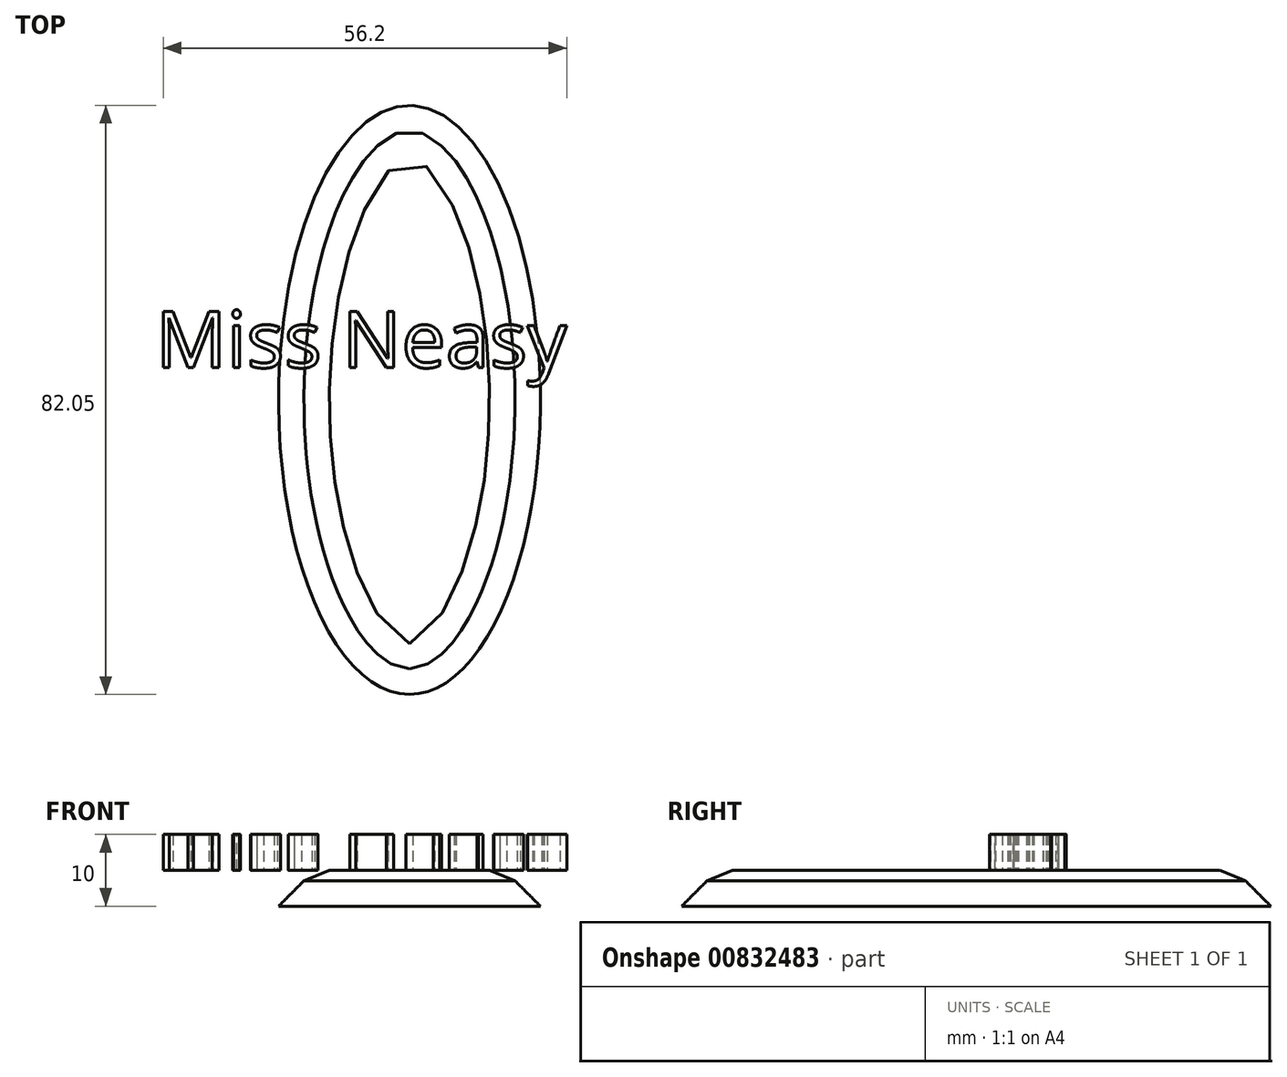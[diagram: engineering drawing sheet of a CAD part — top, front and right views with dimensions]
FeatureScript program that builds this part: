
annotation { "Feature Type Name" : "Feature", "Feature Type Description" : "" }
export const myFeature = defineFeature(function(context is Context, id is Id, definition is map)
    precondition{}
    {
        {
            var Q0;
            Q0=qCreatedBy(makeId("Top.planeOp"),FACE);
            var sketch = newSketch(context, id + "F0", { "sketchPlane" : qUnion([Q0])});
            skEllipse(sketch, "E0", {"center": v(-12.25, 46.89) * mm, "majorRadius": 41.03 * mm, "minorRadius": 18.23 * mm, "majorAxis": v(0, -1)});
            skSolve(sketch);
        }
        {
            var Q0;
            Q0=makeQuery(id+"F0.imprint","IMPRINT",FACE,{"disambiguationData":[TD([[makeQuery(id+"F0.imprint","IMPRINT",EDGE,{"derivedFrom":sQuery(id+"F0.wireOp",EDGE,"E0")}),1.0]])]});
            var sketch = newSketch(context, id + "F1", { "sketchPlane" : qUnion([Q0])});
            skLineSegment(sketch, "E1", {"start": v(-29.07, 38.27) * mm, "end": v(-13.53, -50.59) * mm});
            skLineSegment(sketch, "E2", {"start": v(-13.53, -50.59) * mm, "end": v(6.03, 41.56) * mm});
            skLineSegment(sketch, "E3", {"start": v(6.03, 41.56) * mm, "end": v(-29.07, 38.27) * mm});
            skSolve(sketch);
        }
        {
            var Q0;
            {var subQ0=sQuery(id+"F1.wireOp",EDGE,"E2");var subQ1=sQuery(id+"F1.wireOp",EDGE,"E1");var subQ2=makeQuery(id+"F1.imprint","INTERSECT",VERTEX,{"derivedFrom":[subQ1,subQ0]});Q0=makeQuery(id+"F1.imprint","IMPRINT",FACE,{"disambiguationData":[TD([[makeQuery(id+"F1.imprint","IMPRINT",EDGE,{"disambiguationData":[TD([[subQ2,1.0]])],"derivedFrom":subQ1}),1.0]])]});}
            var sketch = newSketch(context, id + "F2", { "sketchPlane" : qUnion([Q0])});
            skSolve(sketch);
        }
        {
            var Q0;
            {var subQ0=sQuery(id+"F1.wireOp",EDGE,"E2");var subQ1=sQuery(id+"F1.wireOp",EDGE,"E1");var subQ2=makeQuery(id+"F1.imprint","INTERSECT",VERTEX,{"derivedFrom":[subQ1,subQ0]});Q0=makeQuery(id+"F2.imprint","IMPRINT",FACE,{"disambiguationData":[TD([[makeQuery(id+"F2.imprint","IMPRINT",EDGE,{"derivedFrom":makeQuery(id+"F1.imprint","IMPRINT",EDGE,{"disambiguationData":[TD([[subQ2,1.0]])],"derivedFrom":subQ1})}),1.0]])]});}
            var Q1;
            Q1=makeQuery(id+"F0.imprint","IMPRINT",FACE,{"disambiguationData":[TD([[makeQuery(id+"F0.imprint","IMPRINT",EDGE,{"derivedFrom":sQuery(id+"F0.wireOp",EDGE,"E0")}),1.0]])]});
            extrude(context, id + "F3", {"entities" : qUnion([Q0, Q1]), "depth" : 5 * mm, "offsetDistance" : 25 * mm});
        }
        {
            var Q0;
            Q0=makeQuery(id+"F3.opExtrude","CAP_FACE",FACE,{"disambiguationData":[OSD([sQuery(id+"F0.wireOp",EDGE,"E0")])],"isStart":false});
            chamfer(context, id + "F4", {"entities" : qUnion([Q0]), "width" : 5 * mm, "tangentPropagation" : true});
        }
        {
            var Q0;
            Q0=makeQuery(id+"F3.opExtrude","CAP_FACE",FACE,{"disambiguationData":[OSD([sQuery(id+"F0.wireOp",EDGE,"E0"),sQuery(id+"F1.wireOp",EDGE,"E1"),sQuery(id+"F1.wireOp",EDGE,"E2")])],"isStart":false});
            chamfer(context, id + "F5", {"entities" : qUnion([Q0]), "width" : 5 * mm, "tangentPropagation" : true});
        }
        {
            var Q0;
            Q0=makeQuery(id+"F3.opExtrude","CAP_FACE",FACE,{"disambiguationData":[OSD([sQuery(id+"F0.wireOp",EDGE,"E0")])],"isStart":false});
            var sketch = newSketch(context, id + "F6", { "sketchPlane" : qUnion([Q0])});
            skText(sketch, "E4", { "text": "Miss Neasy ", "fontName": "OpenSans-Regular.ttf"});
            const initialGuessF6  = {"E4": [-0.04763, 0.05139, 1, 0, 0.0079]};
            skSetInitialGuess(sketch, initialGuessF6);
            skSolve(sketch);
        }
        {
            var Q0;
            Q0 = qSketchRegion(id + "F6", true);
            extrude(context, id + "F7", {"entities" : qUnion([Q0]), "operationType" : NewBodyOperationType.ADD, "depth" : 5 * mm, "offsetDistance" : 25 * mm});
        }
    });
